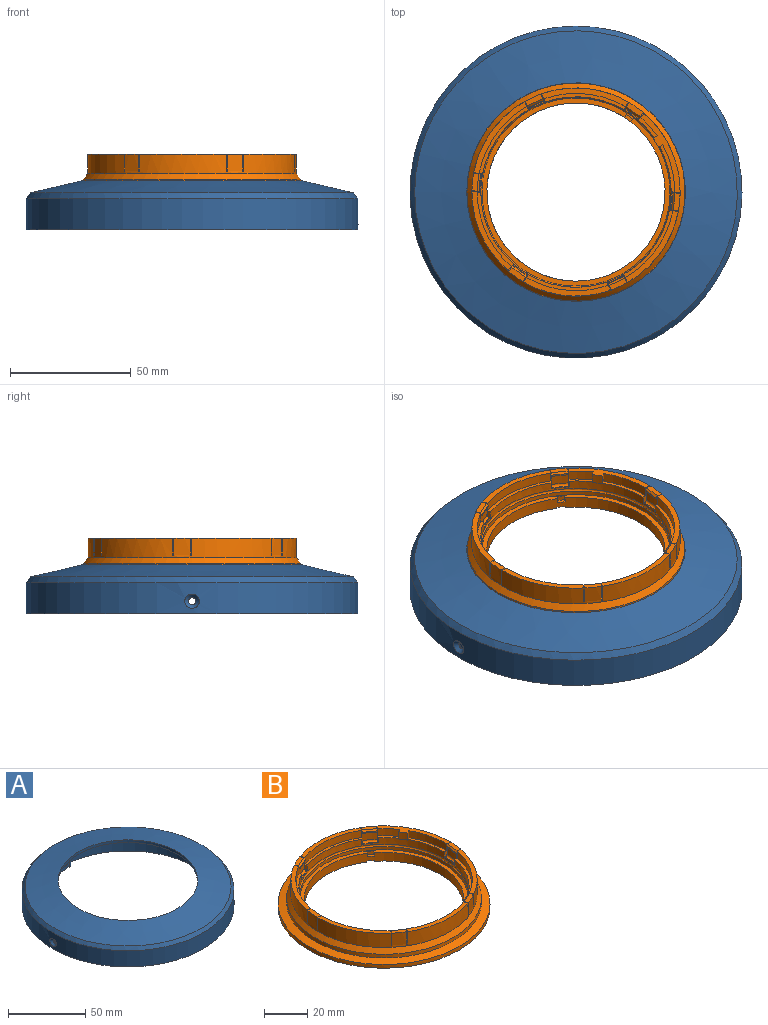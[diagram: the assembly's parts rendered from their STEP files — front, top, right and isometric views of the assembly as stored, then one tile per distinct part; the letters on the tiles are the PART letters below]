
ASSEMBLY  parts=2 mates=1
PART A: 57 faces, bbox 137.7x137.7x20.3 mm
  f0: cylinder r=63.1mm len=126.2mm, axis (0,0,1), area 5272.2mm2, adj f1,f7,f9,f17,f19,f20,f21,f22
  f1: plane 126.2x126.2mm, normal (0,0,-1), area 758.6mm2, adj f0,f2,f3,f4,f8,f10,f14,f19
  f2: cylinder r=57.6mm len=21.49mm, axis (0,0,1), area 252.5mm2, adj f1,f11,f25,f26,f27,f28,f38,f44
  f3: cylinder r=61.6mm len=118.36mm, axis (0,0,1), area 2337mm2, adj f1,f12,f42,f43,f52
  f4: cylinder r=61.6mm len=118.36mm, axis (0,0,1), area 2337mm2, adj f1,f12,f40,f46,f51
  f5: cylinder r=68.85mm len=137.7mm, axis (0,0,1), area 5495.4mm2, adj f16,f18,f49,f50
  f6: cylinder r=66.85mm len=133.7mm, axis (0,0,1), area 5866.2mm2, adj f16,f17,f47,f48
  f7: plane 2.39x1.25mm, normal (0.98,0.22,0), area 3.1mm2, adj f0,f8,f21,f33
  f8: plane 11.5x7.32mm, normal (0.22,-0.98,0), area 57.7mm2, adj f1,f7,f19,f20,f21,f29,f30,f31
  f9: plane 2.39x1.25mm, normal (-0.98,-0.22,0), area 3.1mm2, adj f0,f10,f24,f35
  f10: plane 11.5x7.32mm, normal (-0.22,0.98,0), area 57.7mm2, adj f1,f9,f22,f23,f24,f25,f26,f27
  f11: plane 29.61x6.66mm, normal (0,0,1), area 102.7mm2, adj f2,f12,f43,f44,f45,f46
  f12: cone r=40.93mm half-angle=76.8deg, axis (0,0,-1), area 5610.5mm2, adj f3,f4,f11,f13,f40,f42,f43,f46
  f13: plane 29.61x6.66mm, normal (0,0,1), area 102.7mm2, adj f12,f14,f39,f40,f41,f42
  f14: cylinder r=57.6mm len=21.49mm, axis (0,0,1), area 249.5mm2, adj f1,f13,f29,f30,f31,f32,f37,f39
  f15: cone r=43.17mm half-angle=76.8deg, axis (0,0,-1), area 7816.3mm2, adj f18,f53
  f16: plane 137.7x137.7mm, normal (0,0,-1), area 852.6mm2, adj f5,f6
  f17: plane 133.7x133.7mm, normal (0,0,-1), area 1530.9mm2, adj f0,f6
  f18: cone r=66.9mm half-angle=38.4deg, axis (0,0,-1), area 1336.5mm2, adj f5,f15
  f19: plane 2.39x0.53mm, normal (0.98,0.22,0), area 0.6mm2, adj f0,f1,f8,f34
  f20: plane 11.5x2.39mm, normal (-0.98,-0.22,0), area 28.2mm2, adj f0,f1,f8,f21
  f21: plane 5.41x3.48mm, normal (0,0,-1), area 12.4mm2, adj f0,f7,f8,f20
  f22: plane 11.5x2.39mm, normal (0.98,0.22,0), area 28.2mm2, adj f0,f1,f10,f24
  f23: plane 2.39x0.53mm, normal (-0.98,-0.22,0), area 0.6mm2, adj f0,f1,f10,f36
  f24: plane 5.41x3.48mm, normal (0,0,-1), area 12.4mm2, adj f0,f9,f10,f22
  f25: plane 5x2.96mm, normal (0.98,0.22,0), area 15.2mm2, adj f2,f10,f26,f27
  f26: plane 11.26x6.47mm, normal (0,0,-1), area 53.2mm2, adj f0,f2,f10,f25,f35,f38
  f27: plane 13.77x6.47mm, normal (0,0,1), area 67mm2, adj f0,f2,f10,f25,f28,f36
  f28: plane 5.48x2.5mm, normal (-0.99,0.1,0), area 13.8mm2, adj f0,f2,f27,f38
  f29: plane 12.52x6.47mm, normal (0,0,-1), area 60.1mm2, adj f0,f8,f14,f31,f33,f37
  f30: plane 15.02x6.47mm, normal (0,0,1), area 73.8mm2, adj f0,f8,f14,f31,f32,f34
  f31: plane 5x2.96mm, normal (-0.98,-0.22,0), area 15.2mm2, adj f8,f14,f29,f30
  f32: plane 5.48x2.5mm, normal (0.99,-0.1,0), area 13.8mm2, adj f0,f14,f30,f37
  f33: cylinder r=2.5mm len=2.97mm, axis (-0.22,0.98,0), area 9.3mm2, adj f0,f7,f8,f29
  f34: cylinder r=2.5mm len=2.97mm, axis (0.22,-0.98,0), area 9.3mm2, adj f0,f8,f19,f30
  f35: cylinder r=2.5mm len=2.97mm, axis (0.22,-0.98,0), area 9.3mm2, adj f0,f9,f10,f26
  f36: cylinder r=2.5mm len=2.97mm, axis (-0.22,0.98,0), area 9.3mm2, adj f0,f10,f23,f27
  f37: cylinder r=2.5mm len=5.91mm, axis (0.1,0.99,0), area 21.7mm2, adj f0,f14,f29,f32
  f38: cylinder r=2.5mm len=5.97mm, axis (-0.1,-0.99,0), area 21.7mm2, adj f0,f2,f26,f28
  f39: cylinder r=2mm len=14.5mm, axis (0,0,1), area 44.6mm2, adj f1,f13,f14,f40
  f40: cylinder r=2mm len=14.5mm, axis (0,0,1), area 46.5mm2, adj f1,f4,f12,f13,f39
  f41: cylinder r=2mm len=14.5mm, axis (0,0,1), area 44.6mm2, adj f1,f13,f14,f42
  f42: cylinder r=2mm len=14.5mm, axis (0,0,1), area 46.5mm2, adj f1,f3,f12,f13,f41
  f43: cylinder r=2mm len=14.5mm, axis (0,0,1), area 46.5mm2, adj f1,f3,f11,f12,f44
  f44: cylinder r=2mm len=14.5mm, axis (0,0,1), area 44.6mm2, adj f1,f2,f11,f43,f55
  f45: cylinder r=2mm len=14.5mm, axis (0,0,1), area 44.6mm2, adj f1,f2,f11,f46
  f46: cylinder r=2mm len=14.5mm, axis (0,0,1), area 46.5mm2, adj f1,f4,f11,f12,f45
  f47: cylinder r=1.5mm len=3mm, axis (-1,0,0), area 3.8mm2, adj f6,f49
  f48: cylinder r=1.5mm len=3mm, axis (1,0,0), area 3.8mm2, adj f6,f50
  f49: bspline ~6.02x5.88mm, area 30.6mm2, adj f5,f47
  f50: bspline ~6.02x5.88mm, area 30.6mm2, adj f5,f48
  f51: cylinder r=1.5mm len=3mm, axis (-1,0,0), area 14.1mm2, adj f0,f4
  f52: cylinder r=1.5mm len=3mm, axis (-1,0,0), area 14.1mm2, adj f0,f3
  f53: cylinder r=45.31mm len=90.63mm, axis (0,0,-1), area 584.8mm2, adj f12,f15
  f54: plane 5.49x0.52mm, normal (1,-0.09,0), area 2.8mm2, adj f0,f1,f2,f56
  f55: plane 5.48x0.52mm, normal (-1,0.09,0), area 2.8mm2, adj f0,f1,f44,f56
  f56: plane 5.63x3.56mm, normal (0,0,-1), area 16.7mm2, adj f0,f2,f54,f55
PART B: 127 faces, bbox 98.2x98.2x15.5 mm
  f0: cylinder r=36.95mm len=73.91mm, axis (0,0,1), area 1131.7mm2, adj f2,f119,f120,f121,f123,f124,f125,f126
  f1: cylinder r=49.12mm len=98.25mm, axis (0,0,1), area 635.9mm2, adj f2,f118,f124,f125,f126
  f2: plane 98.25x98.25mm, normal (0,0,-1), area 3246.7mm2, adj f0,f1,f125,f126
  f3: plane 90.25x90.25mm, normal (0,0,1), area 0.7mm2, adj f117,f118
  f4: cone r=43.17mm half-angle=38.4deg, axis (0,0,-1), area 869.2mm2, adj f25,f117
  f5: plane 7x3.36mm, normal (0.91,0.41,0), area 16.7mm2, adj f11,f24,f25,f37,f49,f51,f77,f101
  f6: plane 7x3.67mm, normal (0.1,1,0), area 16.7mm2, adj f11,f19,f25,f32,f52,f54,f75,f102
  f7: plane 7x3mm, normal (-0.81,0.58,0), area 16.7mm2, adj f11,f17,f25,f30,f55,f57,f73,f103
  f8: plane 7x3.36mm, normal (-0.91,-0.41,0), area 16.7mm2, adj f11,f15,f25,f28,f58,f60,f91,f104
  f9: plane 7x3.67mm, normal (-0.1,-1,0), area 16.7mm2, adj f11,f14,f25,f27,f61,f63,f96,f99
  f10: plane 7x3mm, normal (0.81,-0.58,0), area 16.7mm2, adj f11,f13,f25,f26,f64,f66,f98,f100
  f11: cylinder r=39.5mm len=79mm, axis (0,0,1), area 813.1mm2, adj f5,f6,f7,f8,f9,f10,f38,f39
  f12: cylinder r=39mm len=78mm, axis (0,0,1), area 441.1mm2, adj f68,f119
  f13: cylinder r=40.93mm len=5.78mm, axis (0,0,1), area 32.3mm2, adj f10,f64,f65,f115
  f14: cylinder r=40.93mm len=7.07mm, axis (0,0,1), area 32.3mm2, adj f9,f61,f62,f116
  f15: cylinder r=40.93mm len=6.46mm, axis (0,0,1), area 32.3mm2, adj f8,f58,f59,f111
  f16: cylinder r=40.93mm len=33.83mm, axis (0,0,1), area 140.2mm2, adj f29,f38,f72,f92
  f17: cylinder r=40.93mm len=5.78mm, axis (0,0,1), area 32.3mm2, adj f7,f55,f56,f112
  f18: cylinder r=40.93mm len=7.56mm, axis (0,0,1), area 40.7mm2, adj f31,f39,f46,f87
  f19: cylinder r=40.93mm len=7.07mm, axis (0,0,1), area 32.3mm2, adj f6,f52,f53,f113
  f20: cylinder r=40.93mm len=27.67mm, axis (0,0,1), area 140.2mm2, adj f33,f40,f76,f84
  f21: cylinder r=40.93mm len=33.83mm, axis (0,0,1), area 140.2mm2, adj f34,f41,f69,f97
  f22: cylinder r=40.93mm len=30.92mm, axis (0,0,1), area 140.2mm2, adj f35,f42,f81,f95
  f23: cylinder r=40.93mm len=27.67mm, axis (0,0,1), area 140.2mm2, adj f36,f43,f78,f90
  f24: cylinder r=40.93mm len=6.46mm, axis (0,0,1), area 32.3mm2, adj f5,f49,f50,f114
  f25: cylinder r=43.17mm len=86.35mm, axis (0,0,1), area 2140.7mm2, adj f4,f5,f6,f7,f8,f9,f10,f26
  f26: plane 7x5.84mm, normal (0,0,1), area 15.6mm2, adj f10,f25,f65,f100
  f27: plane 7.27x2.77mm, normal (0,0,1), area 15.6mm2, adj f9,f25,f62,f99
  f28: plane 7.33x4.86mm, normal (0,0,1), area 15.6mm2, adj f8,f25,f59,f104
  f29: plane 36.08x7.74mm, normal (0,0,1), area 81.5mm2, adj f16,f25,f72,f92,f94
  f30: plane 7x5.84mm, normal (0,0,1), area 15.6mm2, adj f7,f25,f56,f103
  f31: plane 32.98x16.34mm, normal (0,0,1), area 90.1mm2, adj f18,f25,f45,f46,f47,f48,f74,f87
  f32: plane 7.27x2.77mm, normal (0,0,1), area 15.6mm2, adj f6,f25,f53,f102
  f33: plane 29.72x21.98mm, normal (0,0,1), area 81.5mm2, adj f20,f25,f76,f84,f86
  f34: plane 36.08x7.74mm, normal (0,0,1), area 81.5mm2, adj f21,f25,f69,f71,f97
  f35: plane 32.98x16.34mm, normal (0,0,1), area 81.5mm2, adj f22,f25,f81,f83,f95
  f36: plane 29.72x21.98mm, normal (0,0,1), area 81.5mm2, adj f23,f25,f78,f80,f90
  f37: plane 7.33x4.86mm, normal (0,0,1), area 15.6mm2, adj f5,f25,f50,f101
  f38: plane 33.83x6.66mm, normal (0,0,1), area 48.9mm2, adj f11,f16,f72,f92
  f39: plane 8.31x7.62mm, normal (0,0,1), area 14.1mm2, adj f11,f18,f46,f87
  f40: plane 27.81x20.33mm, normal (0,0,1), area 48.9mm2, adj f11,f20,f76,f84
  f41: plane 33.83x6.66mm, normal (0,0,1), area 48.9mm2, adj f11,f21,f69,f97
  f42: plane 30.92x14.93mm, normal (0,0,1), area 48.9mm2, adj f11,f22,f81,f95
  f43: plane 27.81x20.33mm, normal (0,0,1), area 48.9mm2, adj f11,f23,f78,f90
  f44: plane 4.02x2.76mm, normal (0,0,-1), area 2.3mm2, adj f11,f46,f47,f48
  f45: cylinder r=40.93mm len=19.62mm, axis (0,0,1), area 81.9mm2, adj f31,f48,f67,f74
  f46: plane 4x1.67mm, normal (-0.53,0.85,0), area 7.8mm2, adj f18,f31,f39,f44,f47
  f47: cylinder r=38.97mm len=4mm, axis (0,0,1), area 17.6mm2, adj f31,f44,f46,f48
  f48: plane 4x1.67mm, normal (0.53,-0.85,0), area 7.8mm2, adj f31,f44,f45,f47,f67
  f49: plane 6.71x3.49mm, normal (0,0,-1), area 5mm2, adj f5,f24,f50,f51
  f50: plane 7x3.36mm, normal (-0.91,-0.41,0), area 16.7mm2, adj f11,f24,f25,f37,f49,f51,f70,f101
  f51: plane 6.46x2.94mm, normal (-0.41,0.91,0), area 4.3mm2, adj f5,f49,f50,f101
  f52: plane 7.12x1.27mm, normal (0,0,-1), area 5mm2, adj f6,f19,f53,f54
  f53: plane 7x3.67mm, normal (-0.1,-1,0), area 16.7mm2, adj f11,f19,f25,f32,f52,f54,f85,f102
  f54: plane 7.07x0.68mm, normal (-1,0.1,0), area 4.3mm2, adj f6,f52,f53,f102
  f55: plane 6.13x4.61mm, normal (0,0,-1), area 5mm2, adj f7,f17,f56,f57
  f56: plane 7x3mm, normal (0.81,-0.58,0), area 16.7mm2, adj f11,f17,f25,f30,f55,f57,f88,f103
  f57: plane 5.78x4.12mm, normal (-0.58,-0.81,0), area 4.3mm2, adj f7,f55,f56,f103
  f58: plane 6.71x3.49mm, normal (0,0,-1), area 5mm2, adj f8,f15,f59,f60
  f59: plane 7x3.36mm, normal (0.91,0.41,0), area 16.7mm2, adj f11,f15,f25,f28,f58,f60,f93,f104
  f60: plane 6.46x2.94mm, normal (0.41,-0.91,0), area 4.3mm2, adj f8,f58,f59,f104
  f61: plane 7.12x1.27mm, normal (0,0,-1), area 5mm2, adj f9,f14,f62,f63
  f62: plane 7x3.67mm, normal (0.1,1,0), area 16.7mm2, adj f11,f14,f25,f27,f61,f63,f79,f99
  f63: plane 7.07x0.68mm, normal (1,-0.1,0), area 4.3mm2, adj f9,f61,f62,f99
  f64: plane 6.13x4.61mm, normal (0,0,-1), area 5mm2, adj f10,f13,f65,f66
  f65: plane 7x3mm, normal (-0.81,0.58,0), area 16.7mm2, adj f11,f13,f25,f26,f64,f66,f82,f100
  f66: plane 5.78x4.12mm, normal (0.58,0.81,0), area 4.3mm2, adj f10,f64,f65,f100
  f67: plane 19.62x6.21mm, normal (0,0,1), area 28.5mm2, adj f11,f45,f48,f74
  f68: torus R=38.3mm, axis (0,0,-1), area 281.1mm2, adj f11,f12
  f69: plane 7x1.31mm, normal (0.91,0.42,0), area 4.4mm2, adj f11,f21,f34,f41,f70,f71
  f70: plane 3.47x1.87mm, normal (0,0,1), area 1.3mm2, adj f11,f25,f50,f69,f71
  f71: plane 7x2.05mm, normal (0.91,0.41,0), area 15.8mm2, adj f25,f34,f69,f70
  f72: plane 7x3.01mm, normal (0.81,-0.58,0), area 20.1mm2, adj f11,f16,f25,f29,f38,f73
  f73: plane 3.18x2.45mm, normal (0,0,1), area 1.3mm2, adj f7,f11,f25,f72
  f74: plane 7x3.67mm, normal (-0.1,-1,0), area 20.1mm2, adj f11,f25,f31,f45,f67,f75
  f75: plane 3.68x0.71mm, normal (0,0,1), area 1.3mm2, adj f6,f11,f25,f74
  f76: plane 7x3.36mm, normal (-0.91,-0.41,0), area 20.1mm2, adj f11,f20,f25,f33,f40,f77
  f77: plane 3.53x1.84mm, normal (0,0,1), area 1.3mm2, adj f5,f11,f25,f76
  f78: plane 7x1.43mm, normal (-0.1,-1,0), area 4.4mm2, adj f11,f23,f36,f43,f79,f80
  f79: plane 3.74x0.7mm, normal (0,0,1), area 1.3mm2, adj f11,f25,f62,f78,f80
  f80: plane 7x2.24mm, normal (-0.1,-1,0), area 15.8mm2, adj f25,f36,f78,f79
  f81: plane 7x1.17mm, normal (0.81,-0.58,0), area 4.4mm2, adj f11,f22,f35,f42,f82,f83
  f82: plane 3.23x2.41mm, normal (0,0,1), area 1.3mm2, adj f11,f25,f65,f81,f83
  f83: plane 7x1.83mm, normal (0.81,-0.58,0), area 15.8mm2, adj f25,f35,f81,f82
  f84: plane 7x1.43mm, normal (0.1,1,0), area 4.4mm2, adj f11,f20,f33,f40,f85,f86
  f85: plane 3.74x0.7mm, normal (0,0,1), area 1.3mm2, adj f11,f25,f53,f84,f86
  f86: plane 7x2.24mm, normal (0.1,1,0), area 15.8mm2, adj f25,f33,f84,f85
  f87: plane 7x1.17mm, normal (-0.81,0.58,0), area 4.4mm2, adj f11,f18,f31,f39,f88,f89
  f88: plane 3.23x2.41mm, normal (0,0,1), area 1.3mm2, adj f11,f25,f56,f87,f89
  f89: plane 7x1.83mm, normal (-0.81,0.58,0), area 15.8mm2, adj f25,f31,f87,f88
  f90: plane 7x3.36mm, normal (0.91,0.41,0), area 20.1mm2, adj f11,f23,f25,f36,f43,f91
  f91: plane 3.53x1.84mm, normal (0,0,1), area 1.3mm2, adj f8,f11,f25,f90
  f92: plane 7x1.31mm, normal (-0.91,-0.41,0), area 4.4mm2, adj f11,f16,f29,f38,f93,f94
  f93: plane 3.47x1.86mm, normal (0,0,1), area 1.3mm2, adj f11,f25,f59,f92,f94
  f94: plane 7x2.05mm, normal (-0.91,-0.41,0), area 15.8mm2, adj f25,f29,f92,f93
  f95: plane 7x3.67mm, normal (0.1,1,0), area 20.1mm2, adj f11,f22,f25,f35,f42,f96
  f96: plane 3.68x0.71mm, normal (0,0,1), area 1.3mm2, adj f9,f11,f25,f95
  f97: plane 7x3.01mm, normal (-0.81,0.58,0), area 20.1mm2, adj f11,f21,f25,f34,f41,f98
  f98: plane 3.18x2.45mm, normal (0,0,1), area 1.3mm2, adj f10,f11,f25,f97
  f99: plane 7.14x1.43mm, normal (0.7,-0.07,0.71), area 7.5mm2, adj f9,f27,f62,f63
  f100: plane 6.22x4.73mm, normal (0.41,0.58,0.71), area 7.5mm2, adj f10,f26,f65,f66
  f101: plane 6.77x3.63mm, normal (-0.29,0.64,0.71), area 7.5mm2, adj f5,f37,f50,f51
  f102: plane 7.14x1.43mm, normal (-0.7,0.07,0.71), area 7.5mm2, adj f6,f32,f53,f54
  f103: plane 6.22x4.73mm, normal (-0.41,-0.58,0.71), area 7.5mm2, adj f7,f30,f56,f57
  f104: plane 6.77x3.63mm, normal (0.29,-0.64,0.71), area 7.5mm2, adj f8,f28,f59,f60
  f105: plane 6.03x4.47mm, normal (0,0,1), area 3mm2, adj f10,f11,f65,f115
  f106: plane 7.11x1.11mm, normal (0,0,1), area 3mm2, adj f9,f11,f62,f116
  f107: plane 6.64x3.33mm, normal (0,0,1), area 3mm2, adj f8,f11,f59,f111
  f108: plane 6.03x4.47mm, normal (0,0,1), area 3mm2, adj f7,f11,f56,f112
  f109: plane 7.11x1.11mm, normal (0,0,1), area 3mm2, adj f6,f11,f53,f113
  f110: plane 6.64x3.33mm, normal (0,0,1), area 3mm2, adj f5,f11,f50,f114
  f111: torus R=39.93mm, axis (0,0,1), area 11.2mm2, adj f8,f15,f59,f107
  f112: torus R=39.93mm, axis (0,0,1), area 11.2mm2, adj f7,f17,f56,f108
  f113: torus R=39.93mm, axis (0,0,1), area 11.2mm2, adj f6,f19,f53,f109
  f114: torus R=39.93mm, axis (0,0,1), area 11.2mm2, adj f5,f24,f50,f110
  f115: torus R=39.93mm, axis (0,0,1), area 11.2mm2, adj f10,f13,f65,f105
  f116: torus R=39.93mm, axis (0,0,1), area 11.2mm2, adj f9,f14,f62,f106
  f117: cylinder r=45.12mm len=90.25mm, axis (0,0,1), area 582.6mm2, adj f3,f4
  f118: cone r=49.2mm half-angle=76.8deg, axis (0,0,-1), area 1215.5mm2, adj f1,f3
  f119: plane 78x78mm, normal (0,0,1), area 483mm2, adj f0,f12,f120,f121,f122
  f120: plane 2x1.25mm, normal (0.81,-0.58,0), area 3.1mm2, adj f0,f119,f122,f123
  f121: plane 2x1.25mm, normal (-0.81,0.58,0), area 3.1mm2, adj f0,f119,f122,f123
  f122: plane 2.69x2mm, normal (-0.58,-0.81,0), area 6.6mm2, adj f119,f120,f121,f123
  f123: plane 3.58x3.17mm, normal (0,0,1), area 5mm2, adj f0,f120,f121,f122
  f124: plane 11.98x9.99mm, normal (0,0,-1), area 43.6mm2, adj f0,f1,f125,f126
  f125: plane 9.91x7.07mm, normal (-0.81,0.58,0), area 6.1mm2, adj f0,f1,f2,f124
  f126: plane 9.92x7.07mm, normal (0.81,-0.58,0), area 6.1mm2, adj f0,f1,f2,f124
PLACE A t=(0,250,158.54)mm
PLACE B t=(0,0,159)mm fixed
MATE fastened A.f0 <-> B.f0  axis (0,0,-1) through (0,0,2.09)mm
